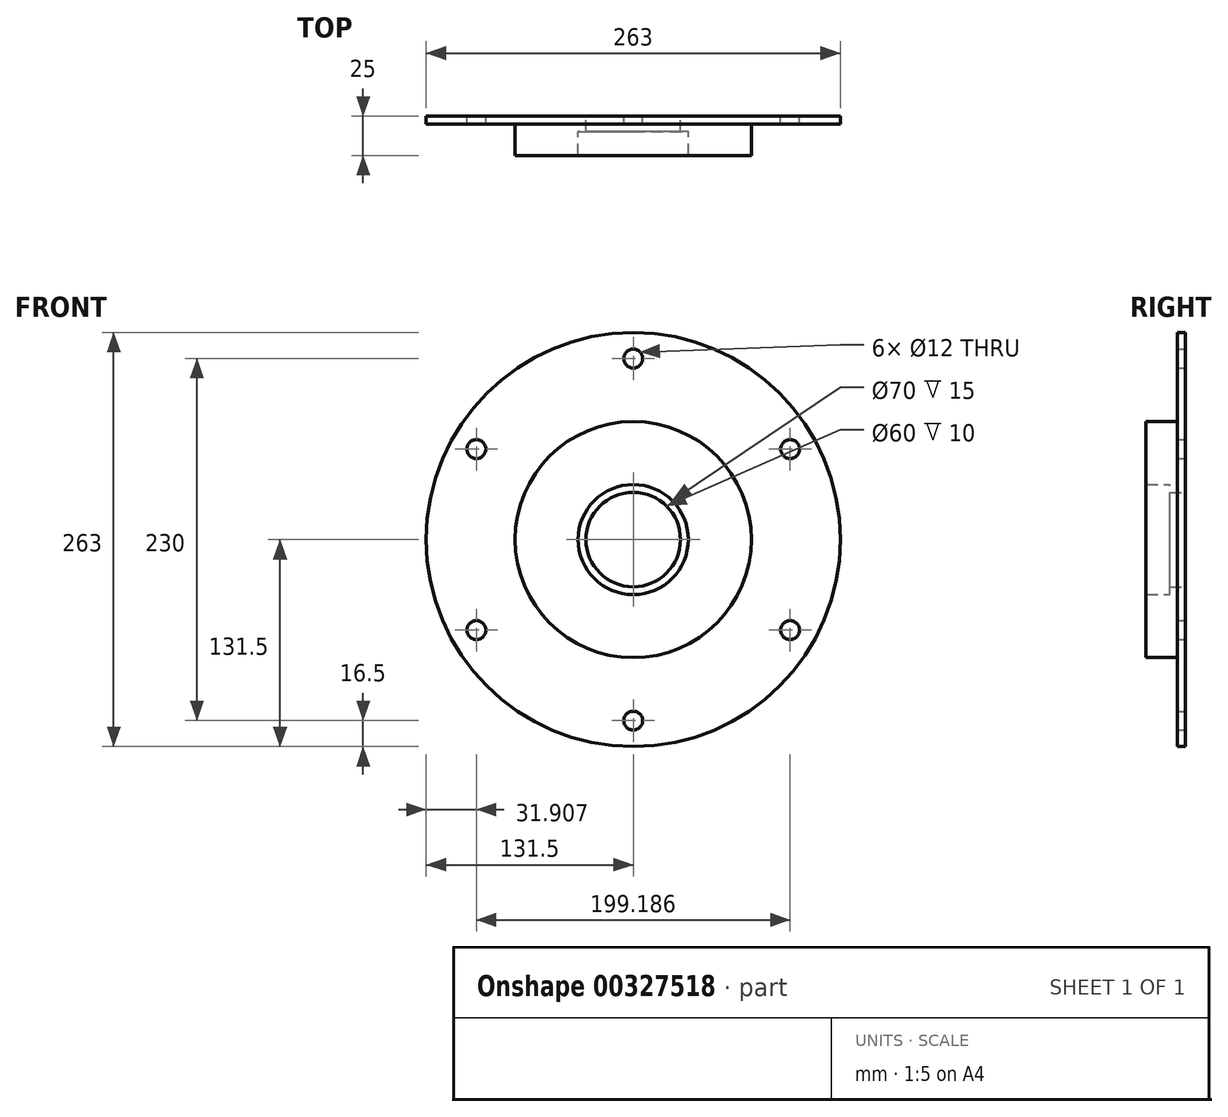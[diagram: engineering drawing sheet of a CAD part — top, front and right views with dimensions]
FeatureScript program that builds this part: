
annotation { "Feature Type Name" : "Feature", "Feature Type Description" : "" }
export const myFeature = defineFeature(function(context is Context, id is Id, definition is map)
    precondition{}
    {
        {
            var Q0;
            Q0=qCreatedBy(makeId("Front.planeOp"),FACE);
            var sketch = newSketch(context, id + "F0", { "sketchPlane" : qUnion([Q0])});
            skCircle(sketch, "E0", {"center": v(0, 0) * mm, "radius": 131.5 * mm});
            skCircle(sketch, "E1", {"center": v(0, 0) * mm, "radius": 75 * mm});
            skCircle(sketch, "E2", {"center": v(0, 0) * mm, "radius": 35 * mm});
            skCircle(sketch, "E3", {"center": v(0, 0) * mm, "radius": 30 * mm});
            skCircle(sketch, "E4", {"center": v(0, 0) * mm, "radius": 115 * mm, "construction": true});
            skLineSegment(sketch, "E5", {"start": v(0, 0) * mm, "end": v(131.5, 0) * mm, "construction": true});
            skLineSegment(sketch, "E6", {"start": v(0, 0) * mm, "end": v(0, 131.5) * mm, "construction": true});
            skLineSegment(sketch, "E7", {"start": v(0, 0) * mm, "end": v(99.6, 57.5) * mm, "construction": true});
            skCircle(sketch, "E8", {"center": v(99.6, 57.5) * mm, "radius": 6 * mm});
            skLineSegment(sketch, "E9.MirrorCS", {"start": v(0, 0) * mm, "end": v(99.6, -57.5) * mm, "construction": true});
            skCircle(sketch, "E10.MirrorC", {"center": v(99.6, -57.5) * mm, "radius": 6 * mm});
            skCircle(sketch, "E11.MirrorC", {"center": v(-99.6, -57.5) * mm, "radius": 6 * mm});
            skCircle(sketch, "E12.MirrorC", {"center": v(-99.6, 57.5) * mm, "radius": 6 * mm});
            skCircle(sketch, "E13.MirrorC", {"center": v(0, 115) * mm, "radius": 6 * mm});
            skCircle(sketch, "E14.MirrorC", {"center": v(0, -115) * mm, "radius": 6 * mm});
            skSolve(sketch);
        }
        {
            var Q0;
            Q0=makeQuery(id+"F0.imprint","IMPRINT",FACE,{"disambiguationData":[TD([[makeQuery(id+"F0.imprint","IMPRINT",EDGE,{"derivedFrom":sQuery(id+"F0.wireOp",EDGE,"E0")}),1.0]])]});
            var Q1;
            {var subQ1=sQuery(id+"F0.wireOp",EDGE,"E1");var subQ17=sQuery(id+"F0.wireOp",EDGE,"E7");var subQ18=makeQuery(id+"F0.imprint","INTERSECT",VERTEX,{"derivedFrom":[subQ1,subQ17]});Q1=makeQuery(id+"F0.imprint","IMPRINT",FACE,{"disambiguationData":[TD([[makeQuery(id+"F0.imprint","IMPRINT",EDGE,{"disambiguationData":[TD([[subQ18,-1.0]])],"derivedFrom":subQ1}),-1.0]])]});}
            var Q2;
            {var subQ1=sQuery(id+"F0.wireOp",EDGE,"E1");var subQ5=sQuery(id+"F0.wireOp",EDGE,"E7");var subQ6=makeQuery(id+"F0.imprint","INTERSECT",VERTEX,{"derivedFrom":[subQ1,subQ5]});Q2=makeQuery(id+"F0.imprint","IMPRINT",FACE,{"disambiguationData":[TD([[makeQuery(id+"F0.imprint","IMPRINT",EDGE,{"disambiguationData":[TD([[subQ6,1.0]])],"derivedFrom":subQ1}),-1.0]])]});}
            var Q3;
            Q3=makeQuery(id+"F0.imprint","IMPRINT",FACE,{"disambiguationData":[TD([[makeQuery(id+"F0.imprint","IMPRINT",EDGE,{"derivedFrom":sQuery(id+"F0.wireOp",EDGE,"E1")}),-1.0]])]});
            extrude(context, id + "F1", {"entities" : qUnion([Q0, Q1, Q2, Q3]), "depth" : 5 * mm});
        }
        {
            var Q0;
            Q0=makeQuery(id+"F0.imprint","IMPRINT",FACE,{"disambiguationData":[TD([[makeQuery(id+"F0.imprint","IMPRINT",EDGE,{"derivedFrom":sQuery(id+"F0.wireOp",EDGE,"E1")}),1.0]])]});
            extrude(context, id + "F2", {"entities" : qUnion([Q0]), "operationType" : NewBodyOperationType.ADD, "depth" : 25 * mm});
        }
        {
            var Q0;
            Q0=makeQuery(id+"F0.imprint","IMPRINT",FACE,{"disambiguationData":[TD([[makeQuery(id+"F0.imprint","IMPRINT",EDGE,{"derivedFrom":sQuery(id+"F0.wireOp",EDGE,"E2")}),1.0]])]});
            extrude(context, id + "F3", {"entities" : qUnion([Q0]), "operationType" : NewBodyOperationType.ADD, "depth" : 10 * mm});
        }
    });
